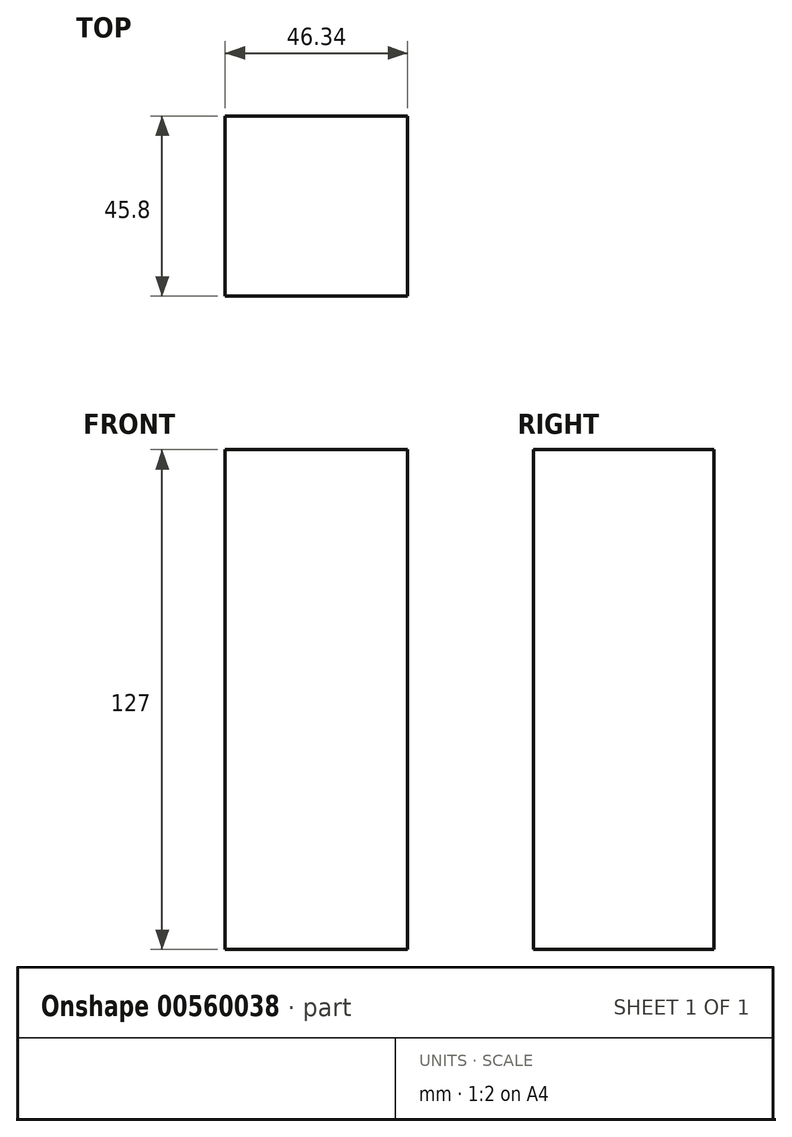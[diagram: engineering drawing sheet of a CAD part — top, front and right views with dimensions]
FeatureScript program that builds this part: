
annotation { "Feature Type Name" : "Feature", "Feature Type Description" : "" }
export const myFeature = defineFeature(function(context is Context, id is Id, definition is map)
    precondition{}
    {
        {
            var Q0;
            Q0=qCreatedBy(makeId("Top.planeOp"),FACE);
            var sketch = newSketch(context, id + "F0", { "sketchPlane" : qUnion([Q0])});
            skLineSegment(sketch, "E0.bottom", {"start": v(0, 0) * mm, "end": v(-46.34, 0) * mm});
            skLineSegment(sketch, "E0.top", {"start": v(0, -45.8) * mm, "end": v(-46.34, -45.8) * mm});
            skLineSegment(sketch, "E0.left", {"start": v(0, 0) * mm, "end": v(0, -45.8) * mm});
            skLineSegment(sketch, "E0.right", {"start": v(-46.34, 0) * mm, "end": v(-46.34, -45.8) * mm});
            skSolve(sketch);
        }
        {
            var Q0;
            Q0 = qSketchRegion(id + "F0", true);
            extrude(context, id + "F1", {"entities" : qUnion([Q0]), "depth" : 127 * mm, "offsetDistance" : 25.4 * mm});
        }
    });
